# Revit family: IS_TonicII_R4358_BIM_DE
name_source: partatom
category: Plumbing Fixtures
revit_build: Autodesk Revit MEP 2016 (Build: 20161004_0715(x64)
units: mm (PartAtom-declared; Revit-internal decimal feet)

## family parameters
Always vertical = No
Cut with Voids When Loaded = No
OmniClass Number = 23.45.05.14.17.11
OmniClass Title = Shower Compartments
Part Type = Normal
Room Calculation Point = No
Round Connector Dimension = Use Diameter
Shared = No
Work Plane-Based = No

## types (2) — shared parameters
Accessories = www.idealstandard.de\ersatzteile
Assembly Code = C1030200
AssetType = Fest
BIMobject category = Accessories
BOSUseNativeGeometries = 1
Brand = Ideal Standard
Brand url = http://www.idealstandard.de
CurrencyUnit = €
CurrentRevision = 1
Date of publishing = 15/09/2017
DurationUnit = Jahr
EAN code = https://3391500572546
Edition number = 1
ExpectedLife = 25
Features = TONIC II furniture handle for vanity unit 597x66mm
IFC Classification = Sanitary Terminal
Installation instructions = http://www.idealstandard.de
InstallationInstructions = www.idealstandard.de\produkte
Manufacturer = www.idealstandard.de\produkte
Manufacturer name = Ideal Standard
ManufacturerURL = http://www.idealstandard.de
NettWeight = 0,55 kg
Nominal height = 30
Nominal width = 597
NominalHeight = 30 mm  [stored 0.0984252 ft]
NominalLength = 66 mm
NominalWidth = 597 mm  [stored 1.95866 ft]
Product Guid = f16fd387-b618-435f-a0bc-f680af952da0
Product SKU = R4358
Product data url = https://bimobject.com
Product family = TONIC II
Product group = Accessories
Product name = TONIC II furniture handle for vanity unit 597x66mm
Product url = http://www.idealstandard.de
ProductInformation = www.idealstandard.de\produkte
QR code = http://bimobject.com
Shape = Sculptured
Size = 30 x 66 x 597mm
Space = Intern
SpareParts = www.idealstandard.de/ersatzteile
Technical description = http://www.idealstandard.de
URL = http://www.idealstandard.de
Uniclass2015Code = Pr_40_30_78_03
Uniclass2015Title = Bathroom cabinets
Uniclass2015Version = Products v1.1
Version = 1
VolumeUnits = Litres
Weight Net (Kg) = 0.55
zero-valued in all types: Cost

## per-type parameters (varying)
| type | BarCode | Color | Description | Finish | MainColor | Model | ModelNumber | ModelReference |
| R4358AA - IS Möbelgriff TONIC II, 597x66x30mm, Chrom | 3391500572553 | Chrome | R4358AA TONIC II furniture handle for vanity unit 597x66mm | Chrome | Chrome | R4358AA | R4358AA | R4358AA TONIC II furniture handle for vanity unit 597x66mm |
| R4358WG - IS Möbelgriff TONIC II, 597x66x30mm, Hgl.weiß lackiert | 3391500572546 | Glossy White | R4358WG TONIC II furniture handle for vanity unit 597x66mm | Glossy White | Glossy White | R4358WG | R4358WG | R4358WG TONIC II furniture handle for vanity unit 597x66mm |

note: [stored X ft] marks values corroborated as IEEE doubles in the binary element streams (Revit-internal decimal feet)

## geometry (parser evidence)
native form markers: Blend x4, Sweep x1
no freeform markers — native parametric forms only
